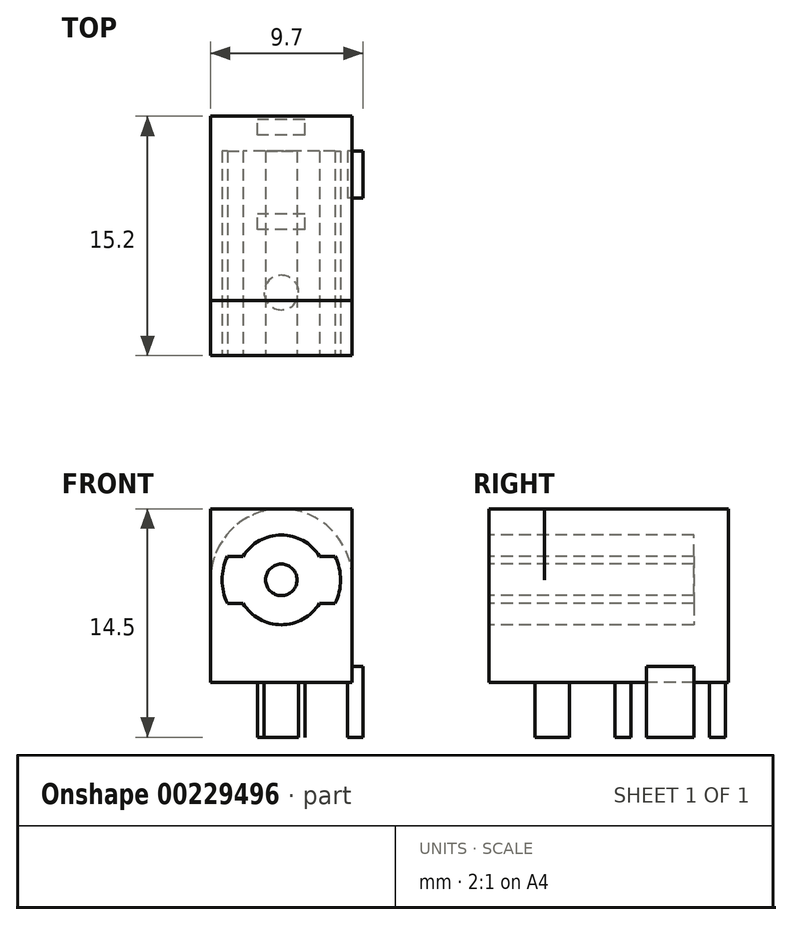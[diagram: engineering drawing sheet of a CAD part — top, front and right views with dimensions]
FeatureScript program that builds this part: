
annotation { "Feature Type Name" : "Feature", "Feature Type Description" : "" }
export const myFeature = defineFeature(function(context is Context, id is Id, definition is map)
    precondition{}
    {
        {
            var Q0;
            Q0=qCreatedBy(makeId("Top.planeOp"),FACE);
            var sketch = newSketch(context, id + "F0", { "sketchPlane" : qUnion([Q0])});
            skLineSegment(sketch, "E0.bottom", {"start": v(4.5, 7.6) * mm, "end": v(-4.5, 7.6) * mm});
            skLineSegment(sketch, "E0.top", {"start": v(4.5, -7.6) * mm, "end": v(-4.5, -7.6) * mm});
            skLineSegment(sketch, "E0.left", {"start": v(4.5, 7.6) * mm, "end": v(4.5, -7.6) * mm});
            skLineSegment(sketch, "E0.right", {"start": v(-4.5, 7.6) * mm, "end": v(-4.5, -7.6) * mm});
            skPoint(sketch, "E0.middle", {"position": v(0, 0) * mm});
            skSolve(sketch);
        }
        {
            var Q0;
            Q0 = qSketchRegion(id + "F0", true);
            extrude(context, id + "F1", {"entities" : qUnion([Q0]), "depth" : 11 * mm});
        }
        {
            var Q0;
            Q0=makeQuery(id+"F1.opExtrude","SWEPT_FACE",FACE,{"disambiguationData":[OSD([sQuery(id+"F0.wireOp",EDGE,"E0.bottom")])]});
            var sketch = newSketch(context, id + "F2", { "sketchPlane" : qUnion([Q0])});
            skArc(sketch, "E1", {"start": v(4.5, 6.5) * mm, "mid": v(0, 11) * mm, "end": v(-4.5, 6.5) * mm});
            skLineSegment(sketch, "E2", {"start": v(-4.5, 6.5) * mm, "end": v(-4.5, 0) * mm});
            skLineSegment(sketch, "E3", {"start": v(-4.5, 0) * mm, "end": v(4.5, 0) * mm});
            skLineSegment(sketch, "E4", {"start": v(4.5, 0) * mm, "end": v(4.5, 6.5) * mm});
            skSolve(sketch);
        }
        {
            var Q0;
            {var subQ0=sQuery(id+"F2.wireOp",EDGE,"E1");var subQ1=sQuery(id+"F0.wireOp",EDGE,"E0.bottom");var subQ4=makeQuery(id+"F1.opExtrude","CAP_EDGE",EDGE,{"disambiguationData":[OSD([subQ1])],"isStart":false});var subQ5=makeQuery(id+"F2.imprint","INTERSECT",VERTEX,{"derivedFrom":[subQ4,subQ0]});Q0=makeQuery(id+"F2.imprint","IMPRINT",FACE,{"disambiguationData":[TD([[makeQuery(id+"F2.imprint","IMPRINT",EDGE,{"disambiguationData":[TD([[subQ5,1.0]])],"derivedFrom":subQ4}),-1.0]])]});}
            var Q1;
            {var subQ0=sQuery(id+"F2.wireOp",EDGE,"E1");var subQ1=sQuery(id+"F0.wireOp",EDGE,"E0.bottom");var subQ4=makeQuery(id+"F1.opExtrude","CAP_EDGE",EDGE,{"disambiguationData":[OSD([subQ1])],"isStart":false});var subQ5=makeQuery(id+"F2.imprint","INTERSECT",VERTEX,{"derivedFrom":[subQ4,subQ0]});Q1=makeQuery(id+"F2.imprint","IMPRINT",FACE,{"disambiguationData":[TD([[makeQuery(id+"F2.imprint","IMPRINT",EDGE,{"disambiguationData":[TD([[subQ5,-1.0]])],"derivedFrom":subQ4}),-1.0]])]});}
            extrude(context, id + "F3", {"entities" : qUnion([Q0, Q1]), "operationType" : NewBodyOperationType.REMOVE, "oppositeDirection" : true, "depth" : (15.2 - 3.5) * mm});
        }
        {
            var Q0;
            Q0=makeQuery(id+"F1.opExtrude","SWEPT_FACE",FACE,{"disambiguationData":[OSD([sQuery(id+"F0.wireOp",EDGE,"E0.top")])]});
            var sketch = newSketch(context, id + "F4", { "sketchPlane" : qUnion([Q0])});
            skCircle(sketch, "E5", {"center": v(0, 6.5) * mm, "radius": 2.85 * mm});
            skArc(sketch, "E6", {"start": v(-3.42, 8) * mm, "mid": v(-3.76, 6.5) * mm, "end": v(-3.42, 5) * mm});
            skArc(sketch, "E7", {"start": v(3.42, 5) * mm, "mid": v(3.76, 6.5) * mm, "end": v(3.42, 8) * mm});
            skLineSegment(sketch, "E8", {"start": v(-3.42, 8) * mm, "end": v(-2.42, 8) * mm});
            skLineSegment(sketch, "E9", {"start": v(-3.42, 5) * mm, "end": v(-2.42, 5) * mm});
            skLineSegment(sketch, "E10", {"start": v(3.42, 5) * mm, "end": v(2.42, 5) * mm});
            skLineSegment(sketch, "E11", {"start": v(3.42, 8) * mm, "end": v(2.42, 8) * mm});
            skCircle(sketch, "E12", {"center": v(0, 6.5) * mm, "radius": 1 * mm});
            skLineSegment(sketch, "E13", {"start": v(-2.42, 8) * mm, "end": v(0, 6.5) * mm, "construction": true});
            skLineSegment(sketch, "E14", {"start": v(0, 6.5) * mm, "end": v(2.42, 8) * mm, "construction": true});
            skLineSegment(sketch, "E15", {"start": v(0, 6.5) * mm, "end": v(2.42, 5) * mm, "construction": true});
            skLineSegment(sketch, "E16", {"start": v(0, 6.5) * mm, "end": v(-2.42, 5) * mm, "construction": true});
            skSolve(sketch);
        }
        {
            var Q0;
            Q0=makeQuery(id+"F4.imprint","IMPRINT",FACE,{"disambiguationData":[TD([[makeQuery(id+"F4.imprint","IMPRINT",EDGE,{"derivedFrom":sQuery(id+"F4.wireOp",EDGE,"E12")}),-1.0]])]});
            var Q1;
            Q1=makeQuery(id+"F4.imprint","IMPRINT",FACE,{"disambiguationData":[TD([[makeQuery(id+"F4.imprint","IMPRINT",EDGE,{"derivedFrom":sQuery(id+"F4.wireOp",EDGE,"E6")}),1.0]])]});
            var Q2;
            Q2=makeQuery(id+"F4.imprint","IMPRINT",FACE,{"disambiguationData":[TD([[makeQuery(id+"F4.imprint","IMPRINT",EDGE,{"derivedFrom":sQuery(id+"F4.wireOp",EDGE,"E7")}),1.0]])]});
            extrude(context, id + "F5", {"entities" : qUnion([Q0, Q1, Q2]), "operationType" : NewBodyOperationType.REMOVE, "oppositeDirection" : true, "depth" : 13 * mm});
        }
        {
            var Q0;
            Q0=makeQuery(id+"F1.opExtrude","CAP_FACE",FACE,{"disambiguationData":[OSD([sQuery(id+"F0.wireOp",EDGE,"E0.bottom"),sQuery(id+"F0.wireOp",EDGE,"E0.top"),sQuery(id+"F0.wireOp",EDGE,"E0.left"),sQuery(id+"F0.wireOp",EDGE,"E0.right")])],"isStart":true});
            var sketch = newSketch(context, id + "F6", { "sketchPlane" : qUnion([Q0])});
            skCircle(sketch, "E17", {"center": v(0, 3.6) * mm, "radius": 1.1 * mm});
            skLineSegment(sketch, "E18.bottom", {"start": v(1.5, -0.4) * mm, "end": v(-1.5, -0.4) * mm});
            skLineSegment(sketch, "E18.top", {"start": v(1.5, -1.4) * mm, "end": v(-1.5, -1.4) * mm});
            skLineSegment(sketch, "E18.left", {"start": v(1.5, -0.4) * mm, "end": v(1.5, -1.4) * mm});
            skLineSegment(sketch, "E18.right", {"start": v(-1.5, -0.4) * mm, "end": v(-1.5, -1.4) * mm});
            skPoint(sketch, "E18.middle", {"position": v(0, -0.9) * mm});
            skLineSegment(sketch, "E19.bottom", {"start": v(1.5, -6.4) * mm, "end": v(-1.5, -6.4) * mm});
            skLineSegment(sketch, "E19.top", {"start": v(1.5, -7.4) * mm, "end": v(-1.5, -7.4) * mm});
            skLineSegment(sketch, "E19.left", {"start": v(1.5, -6.4) * mm, "end": v(1.5, -7.4) * mm});
            skLineSegment(sketch, "E19.right", {"start": v(-1.5, -6.4) * mm, "end": v(-1.5, -7.4) * mm});
            skPoint(sketch, "E19.middle", {"position": v(0, -6.9) * mm});
            skLineSegment(sketch, "E20.bottom", {"start": v(5.2, -5.4) * mm, "end": v(4.2, -5.4) * mm});
            skLineSegment(sketch, "E20.top", {"start": v(5.2, -2.4) * mm, "end": v(4.2, -2.4) * mm});
            skLineSegment(sketch, "E20.left", {"start": v(5.2, -5.4) * mm, "end": v(5.2, -2.4) * mm});
            skLineSegment(sketch, "E20.right", {"start": v(4.2, -5.4) * mm, "end": v(4.2, -2.4) * mm});
            skPoint(sketch, "E20.middle", {"position": v(4.7, -3.9) * mm});
            skSolve(sketch);
        }
        {
            var Q0;
            Q0 = qSketchRegion(id + "F6", true);
            extrude(context, id + "F7", {"entities" : qUnion([Q0]), "operationType" : NewBodyOperationType.ADD, "depth" : 3.5 * mm, "hasSecondDirection" : true, "secondDirectionOppositeDirection" : true, "secondDirectionDepth" : 1 * mm});
        }
    });
